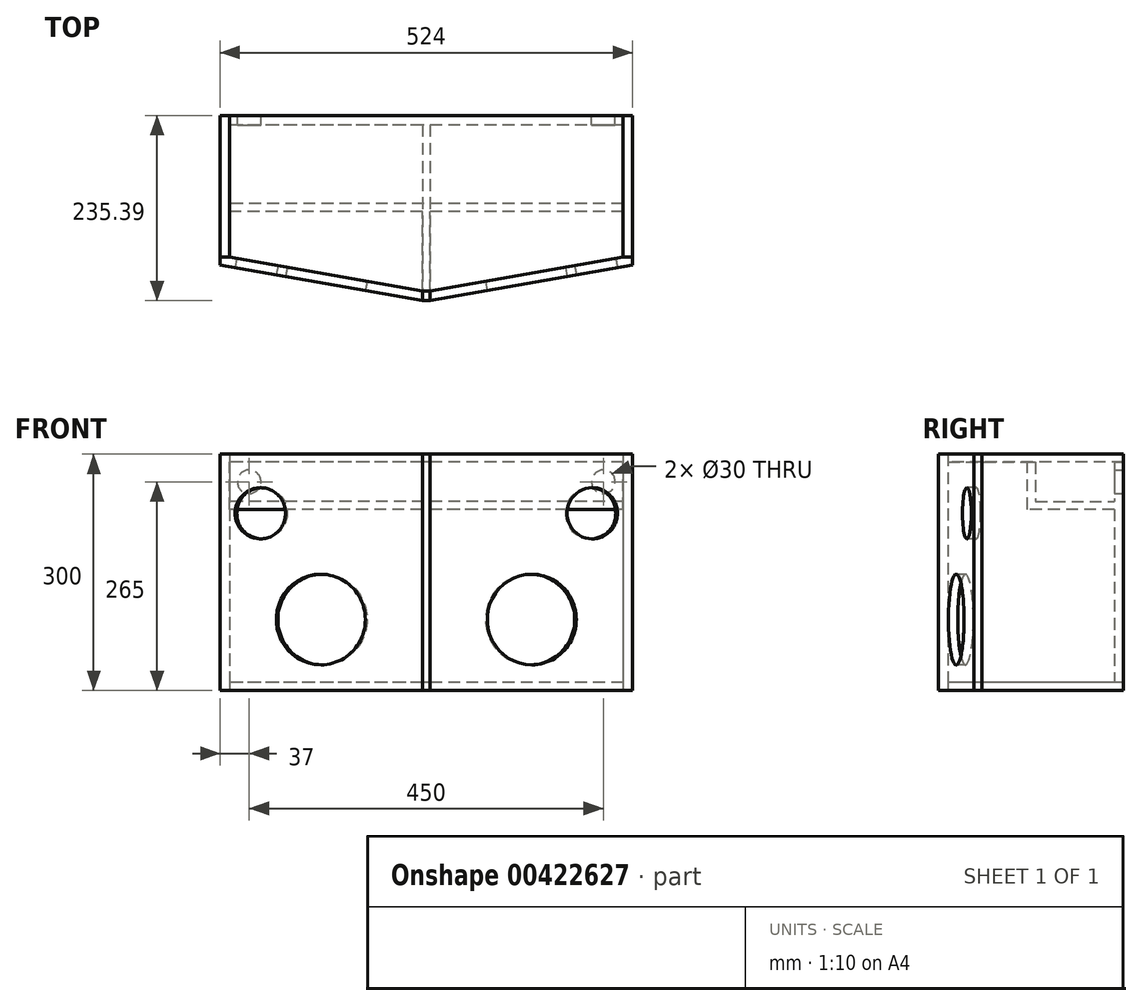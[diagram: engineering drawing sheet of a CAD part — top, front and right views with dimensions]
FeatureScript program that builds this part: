
annotation { "Feature Type Name" : "Feature", "Feature Type Description" : "" }
export const myFeature = defineFeature(function(context is Context, id is Id, definition is map)
    precondition{}
    {
        {
            var Q0;
            Q0=qCreatedBy(makeId("Top.planeOp"),FACE);
            var sketch = newSketch(context, id + "F0", { "sketchPlane" : qUnion([Q0])});
            skLineSegment(sketch, "E0", {"start": v(0, 0) * mm, "end": v(500, 0) * mm});
            skLineSegment(sketch, "E1", {"start": v(0, 0) * mm, "end": v(0, -180) * mm});
            skLineSegment(sketch, "E2", {"start": v(0, -180) * mm, "end": v(245, -223.2) * mm});
            skLineSegment(sketch, "E3", {"start": v(500, 0) * mm, "end": v(500, -180) * mm});
            skLineSegment(sketch, "E4", {"start": v(500, -180) * mm, "end": v(255, -223.2) * mm});
            skLineSegment(sketch, "E5", {"start": v(245, -223.2) * mm, "end": v(255, -223.2) * mm});
            skLineSegment(sketch, "E6", {"start": v(0, 0) * mm, "end": v(-12, 0) * mm});
            skLineSegment(sketch, "E7", {"start": v(-12, 0) * mm, "end": v(-12, -180) * mm});
            skLineSegment(sketch, "E8", {"start": v(-12, -180) * mm, "end": v(0, -180) * mm});
            skLineSegment(sketch, "E9", {"start": v(0, -12) * mm, "end": v(500, -12) * mm, "construction": true});
            skLineSegment(sketch, "E10", {"start": v(245, -223.2) * mm, "end": v(242.92, -235.02) * mm, "construction": true});
            skLineSegment(sketch, "E11", {"start": v(242.92, -235.02) * mm, "end": v(-13.72, -189.77) * mm, "construction": true});
            skLineSegment(sketch, "E12", {"start": v(-12, -180) * mm, "end": v(-12, -190.07) * mm});
            skLineSegment(sketch, "E13", {"start": v(-12, -190.07) * mm, "end": v(242.92, -235.02) * mm});
            skLineSegment(sketch, "E14", {"start": v(0, -180) * mm, "end": v(-11.64, -177.95) * mm, "construction": true});
            skLineSegment(sketch, "E15", {"start": v(-13.72, -189.77) * mm, "end": v(-11.64, -177.95) * mm, "construction": true});
            skLineSegment(sketch, "E16", {"start": v(242.92, -235.02) * mm, "end": v(245, -235.39) * mm, "construction": true});
            skLineSegment(sketch, "E17", {"start": v(245, -223.2) * mm, "end": v(245, -235.39) * mm});
            skLineSegment(sketch, "E18", {"start": v(245, -235.39) * mm, "end": v(247.08, -223.57) * mm, "construction": true});
            skLineSegment(sketch, "E19", {"start": v(245, -223.2) * mm, "end": v(247.08, -223.57) * mm, "construction": true});
            skLineSegment(sketch, "E20", {"start": v(250, -223.2) * mm, "end": v(250, -12) * mm, "construction": true});
            skLineSegment(sketch, "E21.MirrorCS", {"start": v(255, -235.39) * mm, "end": v(252.92, -223.57) * mm, "construction": true});
            skLineSegment(sketch, "E22.MirrorCS", {"start": v(255, -223.2) * mm, "end": v(252.92, -223.57) * mm, "construction": true});
            skLineSegment(sketch, "E23.MirrorCS", {"start": v(255, -223.2) * mm, "end": v(255, -235.39) * mm});
            skLineSegment(sketch, "E24.MirrorCS", {"start": v(257.08, -235.02) * mm, "end": v(255, -235.39) * mm, "construction": true});
            skLineSegment(sketch, "E25.MirrorCS", {"start": v(255, -223.2) * mm, "end": v(257.08, -235.02) * mm, "construction": true});
            skLineSegment(sketch, "E26.MirrorCS", {"start": v(257.08, -235.02) * mm, "end": v(513.72, -189.77) * mm, "construction": true});
            skLineSegment(sketch, "E27.MirrorCS", {"start": v(512, -180) * mm, "end": v(512, -190.07) * mm});
            skLineSegment(sketch, "E28.MirrorCS", {"start": v(513.72, -189.77) * mm, "end": v(511.64, -177.95) * mm, "construction": true});
            skLineSegment(sketch, "E29.MirrorCS", {"start": v(500, -180) * mm, "end": v(511.64, -177.95) * mm, "construction": true});
            skLineSegment(sketch, "E30", {"start": v(-12, -190.07) * mm, "end": v(245, -235.39) * mm});
            skLineSegment(sketch, "E31", {"start": v(245, -235.39) * mm, "end": v(255, -235.39) * mm});
            skLineSegment(sketch, "E32", {"start": v(500, 0) * mm, "end": v(512, 0) * mm});
            skLineSegment(sketch, "E33", {"start": v(512, 0) * mm, "end": v(512, -180) * mm});
            skLineSegment(sketch, "E34", {"start": v(500, -180) * mm, "end": v(512, -180) * mm});
            skLineSegment(sketch, "E35", {"start": v(255, -235.39) * mm, "end": v(512, -190.07) * mm});
            skSolve(sketch);
        }
        {
            var Q0;
            {var subQ3=sQuery(id+"F0.wireOp",EDGE,"E2");Q0=makeQuery(id+"F0.imprint","IMPRINT",FACE,{"disambiguationData":[TD([[makeQuery(id+"F0.imprint","IMPRINT",EDGE,{"derivedFrom":subQ3}),1.0]])]});}
            var Q1;
            Q1=makeQuery(id+"F0.imprint","IMPRINT",FACE,{"disambiguationData":[TD([[makeQuery(id+"F0.imprint","IMPRINT",EDGE,{"derivedFrom":sQuery(id+"F0.wireOp",EDGE,"E5")}),1.0]])]});
            var Q2;
            {var subQ0=sQuery(id+"F0.wireOp",EDGE,"E0");Q2=makeQuery(id+"F0.imprint","IMPRINT",FACE,{"disambiguationData":[TD([[makeQuery(id+"F0.imprint","IMPRINT",EDGE,{"derivedFrom":subQ0}),-1.0]])]});}
            extrude(context, id + "F1", {"entities" : qUnion([Q0, Q1, Q2]), "depth" : 10 * mm});
        }
        {
            var Q0;
            Q0=makeQuery(id+"F0.imprint","IMPRINT",FACE,{"disambiguationData":[TD([[makeQuery(id+"F0.imprint","IMPRINT",EDGE,{"derivedFrom":sQuery(id+"F0.wireOp",EDGE,"E2")}),-1.0]])]});
            extrude(context, id + "F2", {"entities" : qUnion([Q0]), "depth" : 300 * mm});
        }
        {
            var Q0;
            Q0=makeQuery(id+"F0.imprint","IMPRINT",FACE,{"disambiguationData":[TD([[makeQuery(id+"F0.imprint","IMPRINT",EDGE,{"derivedFrom":sQuery(id+"F0.wireOp",EDGE,"E4")}),1.0]])]});
            extrude(context, id + "F3", {"entities" : qUnion([Q0]), "depth" : 300 * mm});
        }
        {
            var Q0;
            Q0=makeQuery(id+"F1.opExtrude","SWEPT_FACE",FACE,{"disambiguationData":[OSD([sQuery(id+"F0.wireOp",EDGE,"E1")])]});
            var sketch = newSketch(context, id + "F4", { "sketchPlane" : qUnion([Q0])});
            skLineSegment(sketch, "E36", {"start": v(0, 0) * mm, "end": v(180, 0) * mm});
            skLineSegment(sketch, "E37", {"start": v(180, 0) * mm, "end": v(180, 300) * mm});
            skLineSegment(sketch, "E38", {"start": v(0, 10) * mm, "end": v(0, 0) * mm});
            skLineSegment(sketch, "E39", {"start": v(180, 300) * mm, "end": v(0, 300) * mm});
            skLineSegment(sketch, "E40", {"start": v(0, 300) * mm, "end": v(0, 10) * mm});
            skSolve(sketch);
        }
        {
            var Q0;
            {var subQ0=sQuery(id+"F4.wireOp",EDGE,"E38");Q0=makeQuery(id+"F4.imprint","IMPRINT",FACE,{"disambiguationData":[TD([[makeQuery(id+"F4.imprint","IMPRINT",EDGE,{"derivedFrom":subQ0}),1.0]])]});}
            var Q1;
            {var subQ3=sQuery(id+"F0.wireOp",EDGE,"E1");var subQ5=makeQuery(id+"F1.opExtrude","CAP_EDGE",EDGE,{"disambiguationData":[OSD([subQ3])],"isStart":false});Q1=makeQuery(id+"F4.imprint","IMPRINT",FACE,{"disambiguationData":[TD([[makeQuery(id+"F4.imprint","IMPRINT",EDGE,{"derivedFrom":subQ5}),-1.0]])]});}
            var Q2;
            {var subQ2=sQuery(id+"F4.wireOp",EDGE,"E39");Q2=makeQuery(id+"F4.imprint","IMPRINT",FACE,{"disambiguationData":[TD([[makeQuery(id+"F4.imprint","IMPRINT",EDGE,{"derivedFrom":subQ2}),1.0]])]});}
            extrude(context, id + "F5", {"entities" : qUnion([Q0, Q1, Q2]), "depth" : 12 * mm});
        }
        {
            var Q0;
            Q0=makeQuery(id+"F1.opExtrude","SWEPT_FACE",FACE,{"disambiguationData":[OSD([sQuery(id+"F0.wireOp",EDGE,"E3")])]});
            var sketch = newSketch(context, id + "F6", { "sketchPlane" : qUnion([Q0])});
            skLineSegment(sketch, "E41", {"start": v(-180, 0) * mm, "end": v(0, 0) * mm});
            skLineSegment(sketch, "E42", {"start": v(0, 0) * mm, "end": v(0, 10) * mm});
            skLineSegment(sketch, "E43", {"start": v(0, 10) * mm, "end": v(0, 300) * mm});
            skLineSegment(sketch, "E44", {"start": v(0, 300) * mm, "end": v(-180, 300) * mm});
            skLineSegment(sketch, "E45", {"start": v(-180, 300) * mm, "end": v(-180, 0) * mm});
            skSolve(sketch);
        }
        {
            var Q0;
            {var subQ1=sQuery(id+"F6.wireOp",EDGE,"E42");Q0=makeQuery(id+"F6.imprint","IMPRINT",FACE,{"disambiguationData":[TD([[makeQuery(id+"F6.imprint","IMPRINT",EDGE,{"derivedFrom":subQ1}),1.0]])]});}
            var Q1;
            {var subQ3=sQuery(id+"F0.wireOp",EDGE,"E3");var subQ5=makeQuery(id+"F1.opExtrude","CAP_EDGE",EDGE,{"disambiguationData":[OSD([subQ3])],"isStart":false});Q1=makeQuery(id+"F6.imprint","IMPRINT",FACE,{"disambiguationData":[TD([[makeQuery(id+"F6.imprint","IMPRINT",EDGE,{"derivedFrom":subQ5}),1.0]])]});}
            var Q2;
            Q2=makeQuery(id+"F6.imprint","IMPRINT",FACE,{"disambiguationData":[TD([[makeQuery(id+"F6.imprint","IMPRINT",EDGE,{"derivedFrom":sQuery(id+"F6.wireOp",EDGE,"E43")}),1.0]])]});
            extrude(context, id + "F7", {"entities" : qUnion([Q0, Q1, Q2]), "depth" : 12 * mm});
        }
        {
            var Q0;
            Q0=makeQuery(id+"F5.opExtrude","CAP_FACE",FACE,{"disambiguationData":[OSD([sQuery(id+"F4.wireOp",EDGE,"E36"),sQuery(id+"F4.wireOp",EDGE,"E37"),sQuery(id+"F4.wireOp",EDGE,"E38"),sQuery(id+"F4.wireOp",EDGE,"E39"),sQuery(id+"F4.wireOp",EDGE,"E40")])],"isStart":true});
            var sketch = newSketch(context, id + "F8", { "sketchPlane" : qUnion([Q0])});
            skLineSegment(sketch, "E46", {"start": v(0, 290) * mm, "end": v(0, 10) * mm});
            skLineSegment(sketch, "E47", {"start": v(-12, 290) * mm, "end": v(-12, 10) * mm});
            skLineSegment(sketch, "E48", {"start": v(0, 290) * mm, "end": v(-12, 290) * mm, "construction": true});
            skLineSegment(sketch, "E49", {"start": v(-12, 290) * mm, "end": v(0, 290) * mm});
            skLineSegment(sketch, "E50", {"start": v(0, 10) * mm, "end": v(-12, 10) * mm});
            skPoint(sketch, "E51.orphan", {"position": v(0, 0) * mm});
            skSolve(sketch);
        }
        {
            var Q0;
            Q0=makeQuery(id+"F8.imprint","IMPRINT",FACE,{"disambiguationData":[TD([[makeQuery(id+"F8.imprint","IMPRINT",EDGE,{"derivedFrom":sQuery(id+"F8.wireOp",EDGE,"E46")}),-1.0]])]});
            extrude(context, id + "F9", {"entities" : qUnion([Q0]), "endBound" : BoundingType.UP_TO_NEXT, "depth" : 500 * mm});
        }
        {
            var Q0;
            Q0=makeQuery(id+"F2.opExtrude","SWEPT_FACE",FACE,{"disambiguationData":[OSD([sQuery(id+"F0.wireOp",EDGE,"E30")])]});
            var sketch = newSketch(context, id + "F10", { "sketchPlane" : qUnion([Q0])});
            skCircle(sketch, "E52", {"center": v(151.19, 90) * mm, "radius": 79 * mm});
            skCircle(sketch, "E53", {"center": v(73.19, 225) * mm, "radius": 45.5 * mm});
            skCircle(sketch, "E54", {"center": v(151.19, 90) * mm, "radius": 57.5 * mm});
            skCircle(sketch, "E55", {"center": v(73.19, 225) * mm, "radius": 32.5 * mm});
            skSolve(sketch);
        }
        {
            var Q0;
            Q0=makeQuery(id+"F10.imprint","IMPRINT",FACE,{"disambiguationData":[TD([[makeQuery(id+"F10.imprint","IMPRINT",EDGE,{"derivedFrom":sQuery(id+"F10.wireOp",EDGE,"E55")}),1.0]])]});
            var Q1;
            Q1=makeQuery(id+"F10.imprint","IMPRINT",FACE,{"disambiguationData":[TD([[makeQuery(id+"F10.imprint","IMPRINT",EDGE,{"derivedFrom":sQuery(id+"F10.wireOp",EDGE,"E54")}),1.0]])]});
            extrude(context, id + "F11", {"entities" : qUnion([Q0, Q1]), "operationType" : NewBodyOperationType.REMOVE, "oppositeDirection" : true, "depth" : 25 * mm});
        }
        {
            var Q0;
            Q0=makeQuery(id+"F3.opExtrude","SWEPT_FACE",FACE,{"disambiguationData":[OSD([sQuery(id+"F0.wireOp",EDGE,"E35")])]});
            var sketch = newSketch(context, id + "F12", { "sketchPlane" : qUnion([Q0])});
            skCircle(sketch, "E56", {"center": v(341.22, 90) * mm, "radius": 79 * mm});
            skCircle(sketch, "E57", {"center": v(419.22, 225) * mm, "radius": 45.5 * mm});
            skCircle(sketch, "E58", {"center": v(419.22, 225) * mm, "radius": 32.5 * mm});
            skCircle(sketch, "E59", {"center": v(341.22, 90) * mm, "radius": 57.5 * mm});
            skSolve(sketch);
        }
        {
            var Q0;
            Q0=makeQuery(id+"F12.imprint","IMPRINT",FACE,{"disambiguationData":[TD([[makeQuery(id+"F12.imprint","IMPRINT",EDGE,{"derivedFrom":sQuery(id+"F12.wireOp",EDGE,"E59")}),1.0]])]});
            var Q1;
            Q1=makeQuery(id+"F12.imprint","IMPRINT",FACE,{"disambiguationData":[TD([[makeQuery(id+"F12.imprint","IMPRINT",EDGE,{"derivedFrom":sQuery(id+"F12.wireOp",EDGE,"E58")}),1.0]])]});
            extrude(context, id + "F13", {"entities" : qUnion([Q0, Q1]), "operationType" : NewBodyOperationType.REMOVE, "oppositeDirection" : true, "depth" : 25 * mm});
        }
        {
            var Q0;
            Q0=makeQuery(id+"F2.opExtrude","SWEPT_FACE",FACE,{"disambiguationData":[OSD([sQuery(id+"F0.wireOp",EDGE,"E17")])]});
            var sketch = newSketch(context, id + "F14", { "sketchPlane" : qUnion([Q0])});
            skLineSegment(sketch, "E60.0", {"start": v(-180, 10) * mm, "end": v(-223.2, 10) * mm});
            skPoint(sketch, "E61.orphan", {"position": v(-223.2, 300) * mm});
            skPoint(sketch, "E62.orphan", {"position": v(-223.2, 0) * mm});
            skLineSegment(sketch, "E63", {"start": v(-180, 10) * mm, "end": v(-12, 10) * mm});
            skLineSegment(sketch, "E64", {"start": v(-12, 10) * mm, "end": v(-12, 290) * mm});
            skLineSegment(sketch, "E65", {"start": v(-235.39, 0) * mm, "end": v(-223.2, 0) * mm});
            skLineSegment(sketch, "E66", {"start": v(-235.39, 0) * mm, "end": v(-235.39, 300) * mm});
            skLineSegment(sketch, "E67", {"start": v(-235.39, 300) * mm, "end": v(-223.2, 300) * mm});
            skLineSegment(sketch, "E68", {"start": v(-223.2, 300) * mm, "end": v(-223.2, 290) * mm});
            skLineSegment(sketch, "E69", {"start": v(-223.2, 290) * mm, "end": v(-12, 290) * mm});
            skLineSegment(sketch, "E70", {"start": v(-223.2, 10) * mm, "end": v(-223.2, 0) * mm});
            skLineSegment(sketch, "E71", {"start": v(-12, 230) * mm, "end": v(-122, 230) * mm});
            skLineSegment(sketch, "E72", {"start": v(-122, 230) * mm, "end": v(-122, 290) * mm});
            skSolve(sketch);
        }
        {
            var Q0;
            Q0=makeQuery(id+"F14.imprint","IMPRINT",FACE,{"disambiguationData":[TD([[makeQuery(id+"F14.imprint","IMPRINT",EDGE,{"derivedFrom":sQuery(id+"F14.wireOp",EDGE,"E60.0")}),-1.0]])]});
            var Q1;
            Q1=makeQuery(id+"F14.imprint","IMPRINT",FACE,{"disambiguationData":[TD([[makeQuery(id+"F14.imprint","IMPRINT",EDGE,{"derivedFrom":sQuery(id+"F14.wireOp",EDGE,"51783792-f3dc-406a-b0d4-1a80337a8a1f.0")}),-1.0]])]});
            var Q2;
            {var subQ0=sQuery(id+"F14.wireOp",EDGE,"qO9AvNXV-f22W-mt5A-qj0W-PzKBXtUGHfyL");Q2=makeQuery(id+"F14.imprint","IMPRINT",FACE,{"disambiguationData":[TD([[makeQuery(id+"F14.imprint","IMPRINT",EDGE,{"derivedFrom":subQ0}),-1.0]])]});}
            var Q3;
            {var subQ0=sQuery(id+"F14.wireOp",EDGE,"wguQVR2a-gTWu-r8EF-Ah0y-C8ykkGN7G5zR");Q3=makeQuery(id+"F14.imprint","IMPRINT",FACE,{"disambiguationData":[TD([[makeQuery(id+"F14.imprint","IMPRINT",EDGE,{"derivedFrom":subQ0}),-1.0]])]});}
            var Q4;
            Q4=makeQuery(id+"F14.imprint","IMPRINT",FACE,{"disambiguationData":[TD([[makeQuery(id+"F14.imprint","IMPRINT",EDGE,{"derivedFrom":sQuery(id+"F14.wireOp",EDGE,"E65")}),-1.0]])]});
            extrude(context, id + "F15", {"entities" : qUnion([Q0, Q1, Q2, Q3, Q4]), "depth" : 10 * mm});
        }
        {
            var Q0;
            Q0=makeQuery(id+"F15.opExtrude","CAP_FACE",FACE,{"disambiguationData":[OSD([sQuery(id+"F14.wireOp",EDGE,"E60.0"),sQuery(id+"F14.wireOp",EDGE,"E63"),sQuery(id+"F14.wireOp",EDGE,"E64"),sQuery(id+"F14.wireOp",EDGE,"E65"),sQuery(id+"F14.wireOp",EDGE,"E66"),sQuery(id+"F14.wireOp",EDGE,"E67"),sQuery(id+"F14.wireOp",EDGE,"E68"),sQuery(id+"F14.wireOp",EDGE,"E69"),sQuery(id+"F14.wireOp",EDGE,"E70"),sQuery(id+"F14.wireOp",EDGE,"E71"),sQuery(id+"F14.wireOp",EDGE,"E72")])],"isStart":false});
            var sketch = newSketch(context, id + "F16", { "sketchPlane" : qUnion([Q0])});
            skLineSegment(sketch, "E73.0", {"start": v(-122, 230) * mm, "end": v(-122, 290) * mm});
            skLineSegment(sketch, "E74", {"start": v(-122, 290) * mm, "end": v(-112, 290) * mm});
            skLineSegment(sketch, "E75", {"start": v(-112, 290) * mm, "end": v(-112, 230) * mm});
            skLineSegment(sketch, "E76", {"start": v(-112, 230) * mm, "end": v(-122, 230) * mm});
            skSolve(sketch);
        }
        {
            var Q0;
            Q0=makeQuery(id+"F16.imprint","IMPRINT",FACE,{"disambiguationData":[TD([[makeQuery(id+"F16.imprint","IMPRINT",EDGE,{"derivedFrom":sQuery(id+"F16.wireOp",EDGE,"E73.0")}),1.0]])]});
            var sketch = newSketch(context, id + "F17", { "sketchPlane" : qUnion([Q0])});
            skLineSegment(sketch, "E77.0", {"start": v(-12, 230) * mm, "end": v(-112, 230) * mm});
            skLineSegment(sketch, "E78.0", {"start": v(-112, 240) * mm, "end": v(-112, 230) * mm});
            skPoint(sketch, "E79.orphan", {"position": v(-122, 230) * mm});
            skLineSegment(sketch, "E80", {"start": v(-112, 240) * mm, "end": v(-12, 240) * mm});
            skLineSegment(sketch, "E81", {"start": v(-12, 240) * mm, "end": v(-12, 230) * mm});
            skSolve(sketch);
        }
        {
            var Q0;
            Q0=makeQuery(id+"F17.imprint","IMPRINT",FACE,{"disambiguationData":[TD([[makeQuery(id+"F17.imprint","IMPRINT",EDGE,{"derivedFrom":sQuery(id+"F17.wireOp",EDGE,"E77.0")}),-1.0]])]});
            extrude(context, id + "F18", {"entities" : qUnion([Q0]), "endBound" : BoundingType.UP_TO_NEXT, "depth" : 25 * mm});
        }
        {
            var Q0;
            Q0=makeQuery(id+"F18.opExtrude","CAP_FACE",FACE,{"disambiguationData":[OSD([sQuery(id+"F17.wireOp",EDGE,"E77.0"),sQuery(id+"F17.wireOp",EDGE,"E78.0"),sQuery(id+"F17.wireOp",EDGE,"E80"),sQuery(id+"F17.wireOp",EDGE,"E81")])],"isStart":true});
            extrude(context, id + "F19", {"entities" : qUnion([Q0]), "operationType" : NewBodyOperationType.ADD, "endBound" : BoundingType.UP_TO_NEXT, "depth" : 25 * mm});
        }
        {
            var Q0;
            Q0 = qSketchRegion(id + "F16", true);
            var Q1;
            Q1=makeQuery(id+"F7.opExtrude","CAP_FACE",FACE,{"disambiguationData":[OSD([sQuery(id+"F6.wireOp",EDGE,"E41"),sQuery(id+"F6.wireOp",EDGE,"E42"),sQuery(id+"F6.wireOp",EDGE,"E43"),sQuery(id+"F6.wireOp",EDGE,"E44"),sQuery(id+"F6.wireOp",EDGE,"E45")])],"isStart":true});
            extrude(context, id + "F20", {"entities" : qUnion([Q0]), "endBound" : BoundingType.UP_TO_SURFACE, "endBoundEntityFace" : qUnion([Q1]), "depth" : 25 * mm});
        }
        {
            var Q0;
            Q0=makeQuery(id+"F20.opExtrude","CAP_FACE",FACE,{"disambiguationData":[OSD([sQuery(id+"F16.wireOp",EDGE,"E73.0"),sQuery(id+"F16.wireOp",EDGE,"E74"),sQuery(id+"F16.wireOp",EDGE,"E75"),sQuery(id+"F16.wireOp",EDGE,"E76")])],"isStart":true});
            var Q1;
            Q1=makeQuery(id+"F5.opExtrude","CAP_FACE",FACE,{"disambiguationData":[OSD([sQuery(id+"F4.wireOp",EDGE,"E36"),sQuery(id+"F4.wireOp",EDGE,"E37"),sQuery(id+"F4.wireOp",EDGE,"E38"),sQuery(id+"F4.wireOp",EDGE,"E39"),sQuery(id+"F4.wireOp",EDGE,"E40")])],"isStart":true});
            extrude(context, id + "F21", {"entities" : qUnion([Q0]), "operationType" : NewBodyOperationType.ADD, "endBound" : BoundingType.UP_TO_SURFACE, "endBoundEntityFace" : qUnion([Q1]), "depth" : 25 * mm});
        }
        {
            var Q0;
            Q0=makeQuery(id+"F1.opExtrude","SWEPT_BODY",BODY,{"disambiguationData":[OSD([sQuery(id+"F0.wireOp",EDGE,"E0"),sQuery(id+"F0.wireOp",EDGE,"E1"),sQuery(id+"F0.wireOp",EDGE,"E2"),sQuery(id+"F0.wireOp",EDGE,"E3"),sQuery(id+"F0.wireOp",EDGE,"E4"),sQuery(id+"F0.wireOp",EDGE,"E5")])]});
            transform(context, id + "F22", {"entities" : qUnion([Q0]), "transformType" : TransformType.TRANSLATION_3D, "dx" : 0 * mm, "dy" : 0 * mm, "dz" : 290 * mm, "makeCopy" : true});
        }
        {
            var Q0;
            Q0=makeQuery(id+"F9.opExtrude","SWEPT_FACE",FACE,{"disambiguationData":[OSD([sQuery(id+"F8.wireOp",EDGE,"E46")])]});
            var sketch = newSketch(context, id + "F23", { "sketchPlane" : qUnion([Q0])});
            skCircle(sketch, "E82", {"center": v(-475, 265) * mm, "radius": 15 * mm});
            skCircle(sketch, "E83", {"center": v(-25, 265) * mm, "radius": 15 * mm});
            skSolve(sketch);
        }
        {
            var Q0;
            Q0=makeQuery(id+"F23.imprint","IMPRINT",FACE,{"disambiguationData":[TD([[makeQuery(id+"F23.imprint","IMPRINT",EDGE,{"derivedFrom":sQuery(id+"F23.wireOp",EDGE,"E82")}),1.0]])]});
            var Q1;
            Q1=makeQuery(id+"F23.imprint","IMPRINT",FACE,{"disambiguationData":[TD([[makeQuery(id+"F23.imprint","IMPRINT",EDGE,{"derivedFrom":sQuery(id+"F23.wireOp",EDGE,"E83")}),1.0]])]});
            extrude(context, id + "F24", {"entities" : qUnion([Q0, Q1]), "operationType" : NewBodyOperationType.REMOVE, "oppositeDirection" : true, "depth" : 25 * mm});
        }
    });
